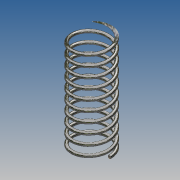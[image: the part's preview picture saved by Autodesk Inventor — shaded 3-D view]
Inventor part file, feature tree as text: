
AUTODESK INVENTOR PART (.ipt)
format: ipt  version: 2015 SP1 (Build 190203100, 203)  size: 437,248 bytes
history: native  units: mm
features: sketch x2, extrude x1, other x1, projected_geometry x1
ambient origin geometry x8: Origin, YZ Plane, XZ Plane, XY Plane, X Axis, Y Axis, Z Axis, Center Point
bodies: Volumenkörper1 (feature_tree)
feature tree (5):
  extrude  "Extrusion1"  TaperAngle=0.0deg  [1 undecoded]
  other  "Spirale1"
  sketch  "Skizze1"  dims[d0=6.0mm d2=0.0mm]
  sketch  "Skizze2"  dims[d3=0.5mm d4=1.5mm d5=15.0mm d6=10.0mm d7=0.0mm d8=90.0deg d9=90.0deg d10=0.0mm d11=0.0mm]
  projected_geometry  "Projizierte Kontur1"
note: 1 required parameter value undecoded (feature->parameter linkage not recoverable at this tier; creation-order binding heuristic only, values carry confidence <= 0.55)
